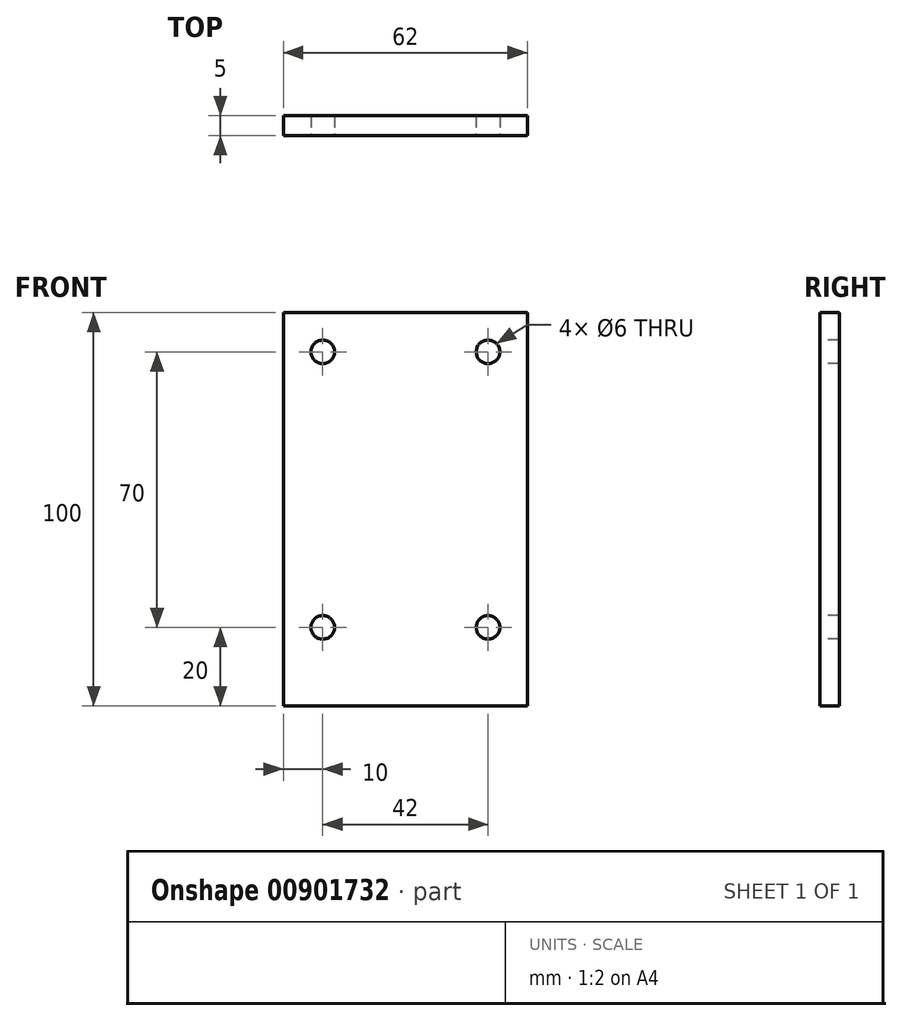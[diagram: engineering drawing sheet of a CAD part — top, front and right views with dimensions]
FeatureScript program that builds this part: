
annotation { "Feature Type Name" : "Feature", "Feature Type Description" : "" }
export const myFeature = defineFeature(function(context is Context, id is Id, definition is map)
    precondition{}
    {
        {
            var Q0;
            Q0=qCreatedBy(makeId("Front.planeOp"),FACE);
            var sketch = newSketch(context, id + "F0", { "sketchPlane" : qUnion([Q0])});
            skLineSegment(sketch, "E0.bottom", {"start": v(0, 0) * mm, "end": v(62, 0) * mm});
            skLineSegment(sketch, "E0.top", {"start": v(0, 100) * mm, "end": v(62, 100) * mm});
            skLineSegment(sketch, "E0.left", {"start": v(0, 0) * mm, "end": v(0, 100) * mm});
            skLineSegment(sketch, "E0.right", {"start": v(62, 0) * mm, "end": v(62, 100) * mm});
            skSolve(sketch);
        }
        {
            var Q0;
            Q0=makeQuery(id+"F0.imprint","IMPRINT",FACE,{"disambiguationData":[TD([[makeQuery(id+"F0.imprint","IMPRINT",EDGE,{"derivedFrom":sQuery(id+"F0.wireOp",EDGE,"E0.bottom")}),1.0]])]});
            extrude(context, id + "F1", {"entities" : qUnion([Q0]), "depth" : 5 * mm, "offsetDistance" : 25 * mm});
        }
        {
            var Q0;
            Q0=makeQuery(id+"F1.opExtrude","CAP_FACE",FACE,{"disambiguationData":[OSD([sQuery(id+"F0.wireOp",EDGE,"E0.bottom"),sQuery(id+"F0.wireOp",EDGE,"E0.top"),sQuery(id+"F0.wireOp",EDGE,"E0.left"),sQuery(id+"F0.wireOp",EDGE,"E0.right")])],"isStart":false});
            var sketch = newSketch(context, id + "F2", { "sketchPlane" : qUnion([Q0])});
            skCircle(sketch, "E1", {"center": v(10, 90) * mm, "radius": 3 * mm});
            skCircle(sketch, "E2", {"center": v(52, 90) * mm, "radius": 3 * mm});
            skCircle(sketch, "E3", {"center": v(10, 20) * mm, "radius": 3 * mm});
            skCircle(sketch, "E4", {"center": v(52, 20) * mm, "radius": 3 * mm});
            skSolve(sketch);
        }
        {
            var Q0;
            Q0 = qSketchRegion(id + "F2", true);
            extrude(context, id + "F3", {"entities" : qUnion([Q0]), "operationType" : NewBodyOperationType.REMOVE, "endBound" : BoundingType.THROUGH_ALL, "oppositeDirection" : true, "depth" : 25 * mm, "offsetDistance" : 25 * mm});
        }
    });
